# Revit family: Showerhead-American_Standard-FloWise-1660.111
name_source: partatom
category: Plumbing Fixtures
units: mm (PartAtom-declared; Revit-internal decimal feet)

## family parameters
Always vertical = No
Cut with Voids When Loaded = No
OmniClass Number = 23.45.05.14.17
OmniClass Title = Showers
Part Type = Normal
Room Calculation Point = No
Round Connector Dimension = Use Diameter
Shared = Yes
Work Plane-Based = Yes

## types (1)
- 1660.111.002
    Assembly Code = D2010710
    CEC Compliant = Yes
    CW Connection = No
    CWFU = 3
    CalGreen Compliant = Yes
    Compliance Certifications = ASME A112.18.1, CSA 125, CUPC Green & EPA WaterSense Certified
    Default Elevation = 0"
    Description = FloWise 3-1/4-in. 1.5 GPM Traditional Water-Saving Shower Head
    Diameter = 3 1/4"
    Finish = Plastic-American Standard-002-Polished Chrome
    Flow Rate = 1.5 gpm
    HW Connection = No
    HWFU = 3
    Length = 3 3/16"
    Manufacturer = American Standard
    Material = Plastic-American Standard-002-Polished Chrome
    Model = 1660.111.002
    Optional 1660.240- Standard Shower Arm and Flange = No
    Optional 1660.241- Modern Shower Arm and Flange = No
    Optional 1660.242- Square Cast Shower Arm = No
    Price = Prices may vary. Please consult Manufacturer Representative for most up-to-date price list.
    Product Documentation Link = https://americanstandard.box.com
    Product Page URL = https://www.americanstandard-us.com
    Revised Date = 07/25/2022
    Tempered Water Connection = Yes
    Tempered Water Connection Diameter = 1/2"
    URL = https://www.americanstandard-us.com
    Vent Connection = No
    WFU = 4
    Waste Connection = No

## geometry (parser evidence)
native form markers: Sweep x2
no freeform markers — native parametric forms only
